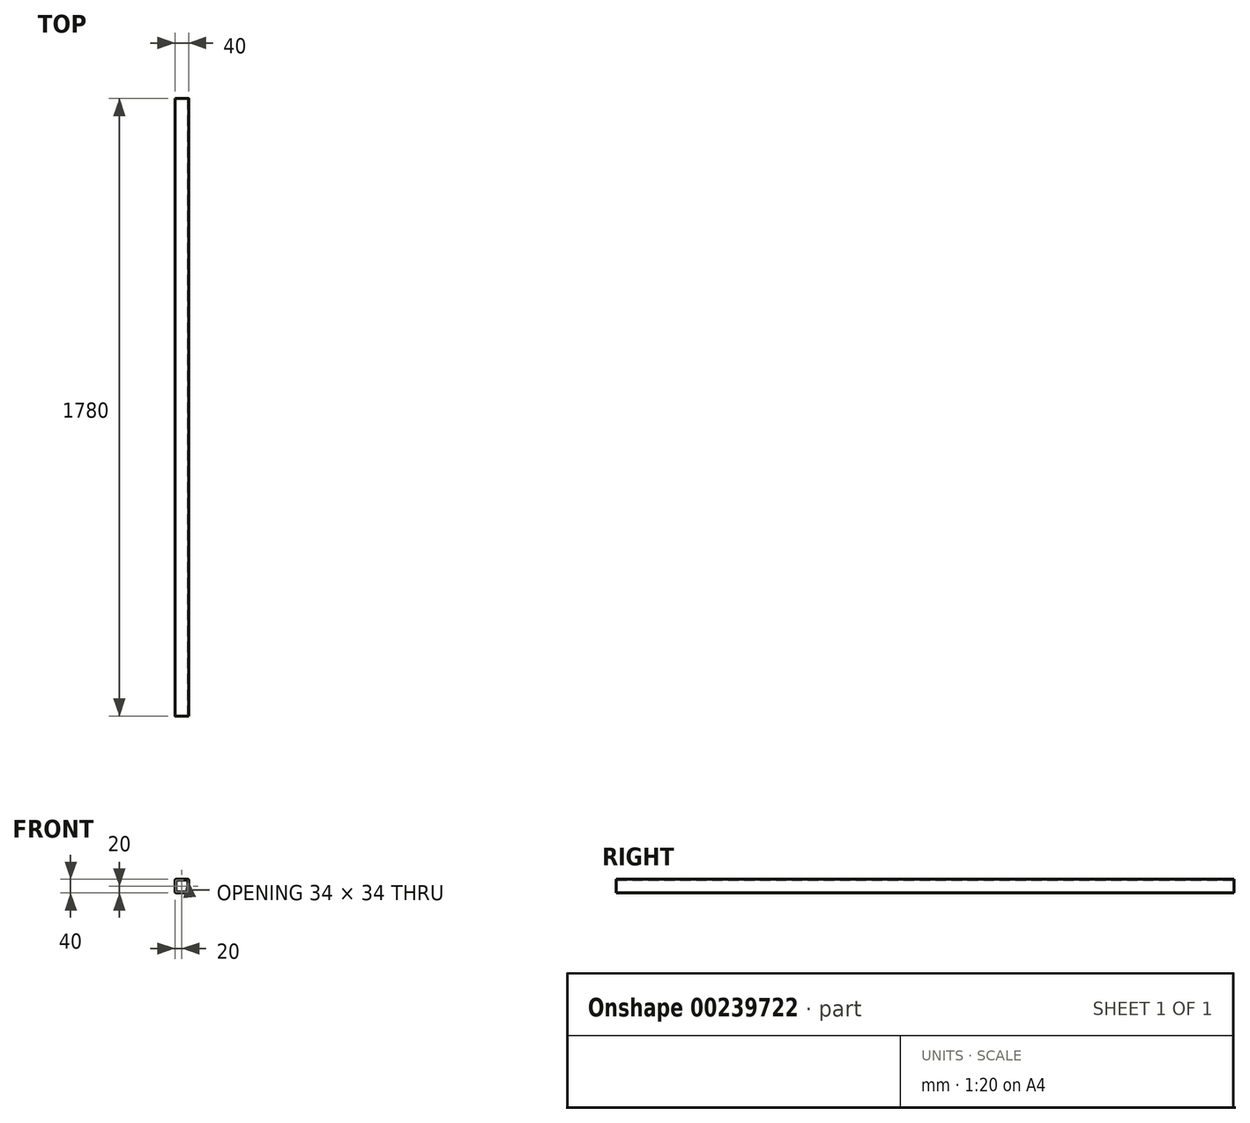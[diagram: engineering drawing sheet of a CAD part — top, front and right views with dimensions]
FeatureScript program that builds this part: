
annotation { "Feature Type Name" : "Feature", "Feature Type Description" : "" }
export const myFeature = defineFeature(function(context is Context, id is Id, definition is map)
    precondition{}
    {
        {
            var Q0;
            Q0=qCreatedBy(makeId("Front.planeOp"),FACE);
            var sketch = newSketch(context, id + "F0", { "sketchPlane" : qUnion([Q0])});
            skLineSegment(sketch, "E0.bottom", {"start": v(16, 20) * mm, "end": v(-16, 20) * mm});
            skLineSegment(sketch, "E0.top", {"start": v(16, -20) * mm, "end": v(-16, -20) * mm});
            skLineSegment(sketch, "E0.left", {"start": v(20, 16) * mm, "end": v(20, -16) * mm});
            skLineSegment(sketch, "E0.right", {"start": v(-20, 16) * mm, "end": v(-20, -16) * mm});
            skPoint(sketch, "E0.middle", {"position": v(0, 0) * mm});
            skPoint(sketch, "E1.visualSharp", {"position": v(-20, 20) * mm});
            skArc(sketch, "E1.filletArc", {"start": v(-16, 20) * mm, "mid": v(-18.83, 18.83) * mm, "end": v(-20, 16) * mm});
            skPoint(sketch, "E2.visualSharp", {"position": v(20, 20) * mm});
            skArc(sketch, "E2.filletArc", {"start": v(20, 16) * mm, "mid": v(18.83, 18.83) * mm, "end": v(16, 20) * mm});
            skPoint(sketch, "E3.visualSharp", {"position": v(20, -20) * mm});
            skArc(sketch, "E3.filletArc", {"start": v(16, -20) * mm, "mid": v(18.83, -18.83) * mm, "end": v(20, -16) * mm});
            skPoint(sketch, "E4.visualSharp", {"position": v(-20, -20) * mm});
            skArc(sketch, "E4.filletArc", {"start": v(-20, -16) * mm, "mid": v(-18.83, -18.83) * mm, "end": v(-16, -20) * mm});
            skLineSegment(sketch, "E5.0", {"start": v(16, 17) * mm, "end": v(-16, 17) * mm});
            skArc(sketch, "E5.1", {"start": v(17, 16) * mm, "mid": v(16.7, 16.7) * mm, "end": v(16, 17) * mm});
            skArc(sketch, "E5.2", {"start": v(-16, 17) * mm, "mid": v(-16.7, 16.7) * mm, "end": v(-17, 16) * mm});
            skLineSegment(sketch, "E5.3", {"start": v(17, 16) * mm, "end": v(17, -16) * mm});
            skLineSegment(sketch, "E5.4", {"start": v(-17, 16) * mm, "end": v(-17, -16) * mm});
            skArc(sketch, "E5.5", {"start": v(-17, -16) * mm, "mid": v(-16.7, -16.7) * mm, "end": v(-16, -17) * mm});
            skLineSegment(sketch, "E5.6", {"start": v(16, -17) * mm, "end": v(-16, -17) * mm});
            skArc(sketch, "E5.7", {"start": v(16, -17) * mm, "mid": v(16.7, -16.7) * mm, "end": v(17, -16) * mm});
            skSolve(sketch);
        }
        {
            var Q0;
            Q0=makeQuery(id+"F0.imprint","IMPRINT",FACE,{"disambiguationData":[TD([[makeQuery(id+"F0.imprint","IMPRINT",EDGE,{"derivedFrom":sQuery(id+"F0.wireOp",EDGE,"E0.bottom")}),1.0]])]});
            extrude(context, id + "F1", {"entities" : qUnion([Q0]), "depth" : 1780 * mm});
        }
    });
